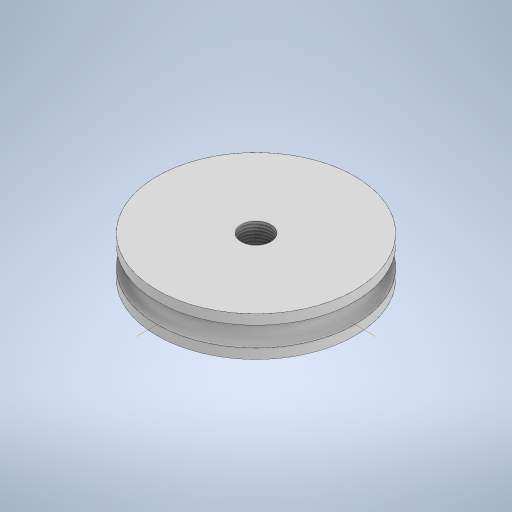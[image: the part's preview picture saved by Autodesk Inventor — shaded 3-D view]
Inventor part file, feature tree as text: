
AUTODESK INVENTOR PART (.ipt)
format: ipt  version: 2023 (Build 270158000, 158)  size: 271,360 bytes
history: native  units: mm
features: sketch x4, extrude x3, other x1, hole x1, thread x1
ambient origin geometry x8: Origin, YZ Plane, XZ Plane, XY Plane, X Axis, Y Axis, Z Axis, Center Point
bodies: Solid1 (feature_tree)
feature tree (10):
  extrude  "Extrusion1"  Depth=10.0mm TaperAngle=0.0deg
  extrude  "Extrusion2"  Depth=5.0mm TaperAngle=0.0deg
  extrude  "Extrusion3"  Depth=5.0mm TaperAngle=0.0deg
  other  "Full Round Fillet1"
  hole  "Hole1"  [1 undecoded]
  thread  "Thread1"  [1 undecoded]
  sketch  "Sketch1"  dims[d0=90.0mm d2=10.0mm d3=0.0mm]
  sketch  "Sketch3"  dims[d5=100.0mm d6=5.0mm d7=0.0mm]
  sketch  "Sketch4"  dims[d8=100.0mm d9=5.0mm d10=0.0mm]
  sketch  "Sketch5"  dims[d11=15.0mm d12=5.94614mm d13=4.0mm d14=2.0mm d15=90.0deg d16=8.0mm d17=20.594885mm d18=51.6mm d19=0.0mm]
note: 2 required parameter values undecoded (feature->parameter linkage not recoverable at this tier; creation-order binding heuristic only, values carry confidence <= 0.55)
